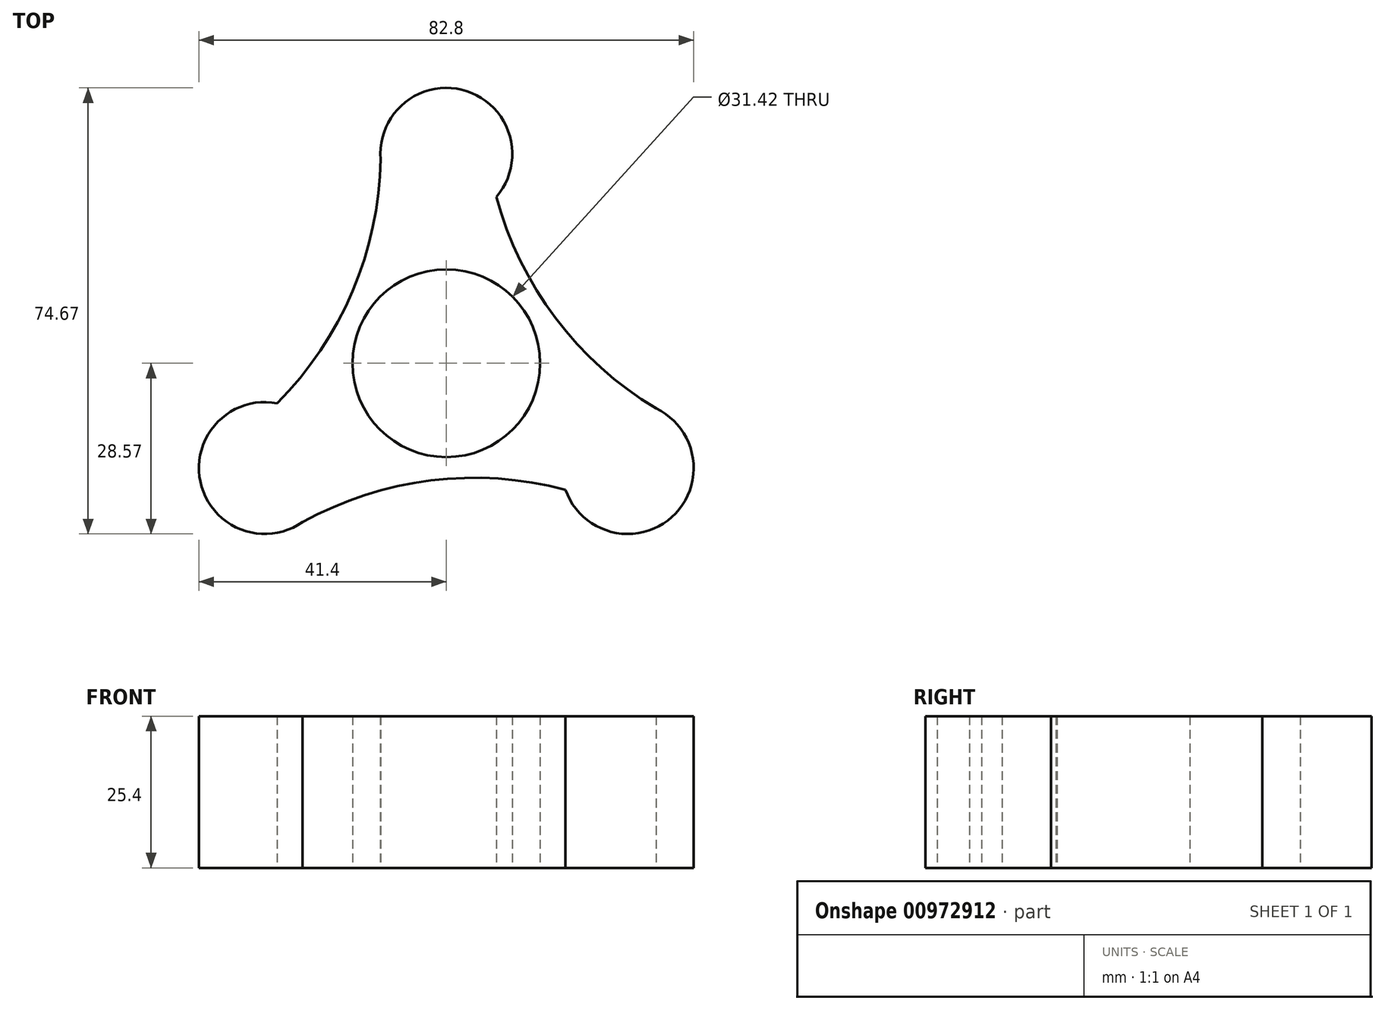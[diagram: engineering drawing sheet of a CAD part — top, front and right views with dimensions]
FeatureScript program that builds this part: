
annotation { "Feature Type Name" : "Feature", "Feature Type Description" : "" }
export const myFeature = defineFeature(function(context is Context, id is Id, definition is map)
    precondition{}
    {
        {
            var Q0;
            Q0=qCreatedBy(makeId("Top.planeOp"),FACE);
            var sketch = newSketch(context, id + "F0", { "sketchPlane" : qUnion([Q0])});
            skCircle(sketch, "E0", {"center": v(0, 0) * mm, "radius": 11.6 * mm});
            skCircle(sketch, "E1", {"center": v(0, 0) * mm, "radius": 15.7 * mm});
            skCircle(sketch, "E2", {"center": v(0, 35.06) * mm, "radius": 11.04 * mm});
            skCircle(sketch, "E3.1.0", {"center": v(-30.37, -17.53) * mm, "radius": 11.04 * mm});
            skCircle(sketch, "E3.2.0", {"center": v(30.37, -17.53) * mm, "radius": 11.04 * mm});
            skArc(sketch, "E4", {"start": v(-28.3, -6.7) * mm, "mid": v(-15.7, 12.06) * mm, "end": v(-11, 34.16) * mm});
            skArc(sketch, "E5.1.0", {"start": v(19.95, -21.17) * mm, "mid": v(-2.6, -19.62) * mm, "end": v(-24.08, -26.6) * mm});
            skArc(sketch, "E5.2.0", {"start": v(8.36, 27.86) * mm, "mid": v(18.3, 7.56) * mm, "end": v(35.08, -7.55) * mm});
            skSolve(sketch);
        }
        {
            var Q0;
            Q0=qSketchRegion(id+"F0",true);
            extrude(context, id + "F1", {"entities" : qUnion([Q0]), "depth" : 25.4 * mm, "offsetDistance" : 25.4 * mm});
        }
    });
